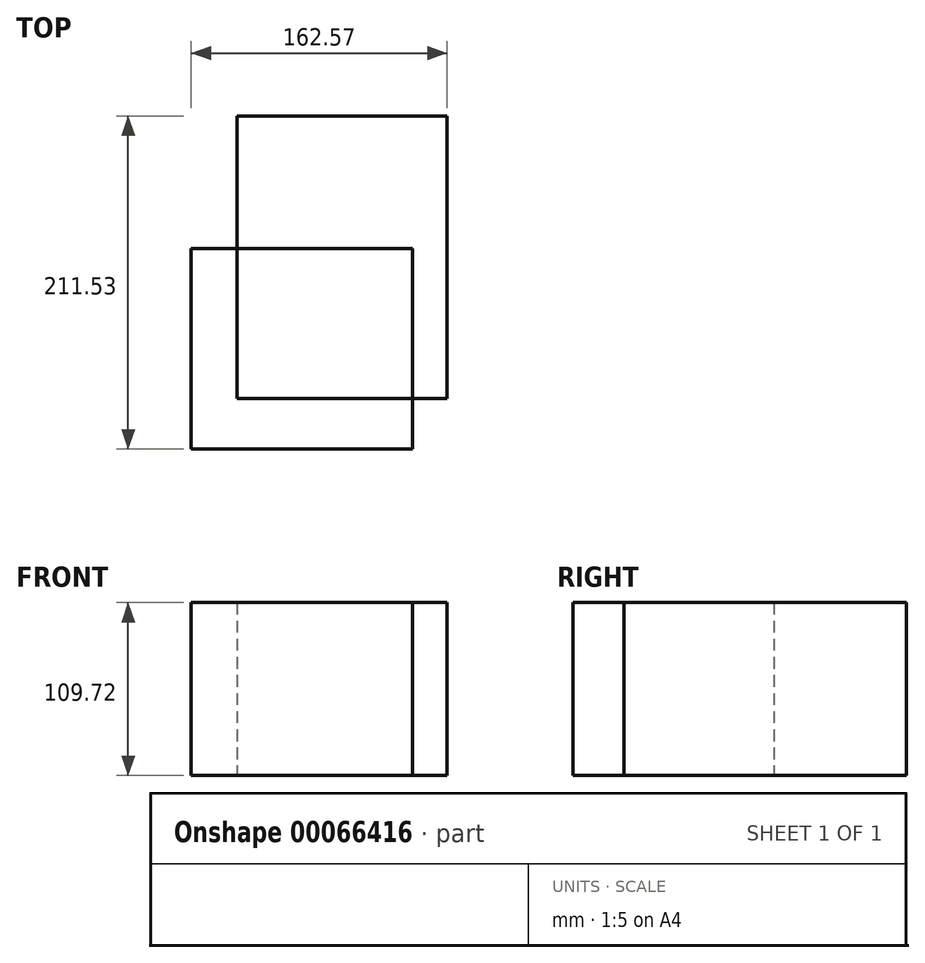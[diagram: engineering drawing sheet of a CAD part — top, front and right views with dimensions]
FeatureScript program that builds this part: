
annotation { "Feature Type Name" : "Feature", "Feature Type Description" : "" }
export const myFeature = defineFeature(function(context is Context, id is Id, definition is map)
    precondition{}
    {
        {
            var Q0;
            Q0=qCreatedBy(makeId("Top.planeOp"),FACE);
            var sketch = newSketch(context, id + "F0", { "sketchPlane" : qUnion([Q0])});
            skLineSegment(sketch, "E0.bottom", {"start": v(-140.53, -61.35) * mm, "end": v(0, -61.35) * mm});
            skLineSegment(sketch, "E0.top", {"start": v(-140.53, -188.84) * mm, "end": v(0, -188.84) * mm});
            skLineSegment(sketch, "E0.left", {"start": v(-140.53, -61.35) * mm, "end": v(-140.53, -188.84) * mm});
            skLineSegment(sketch, "E0.right", {"start": v(0, -61.35) * mm, "end": v(0, -188.84) * mm});
            skLineSegment(sketch, "E1.bottom", {"start": v(-111.48, -156.6) * mm, "end": v(22.04, -156.6) * mm});
            skLineSegment(sketch, "E1.top", {"start": v(-111.48, 22.7) * mm, "end": v(22.04, 22.7) * mm});
            skLineSegment(sketch, "E1.left", {"start": v(-111.48, -156.6) * mm, "end": v(-111.48, 22.7) * mm});
            skLineSegment(sketch, "E1.right", {"start": v(22.04, -156.6) * mm, "end": v(22.04, 22.7) * mm});
            skSolve(sketch);
        }
        {
            var Q0;
            {var subQ2=sQuery(id+"F0.wireOp",EDGE,"E0.top");Q0=makeQuery(id+"F0.imprint","IMPRINT",FACE,{"disambiguationData":[TD([[makeQuery(id+"F0.imprint","IMPRINT",EDGE,{"derivedFrom":subQ2}),1.0]])]});}
            var Q1;
            {var subQ0=sQuery(id+"F0.wireOp",EDGE,"E1.top");Q1=makeQuery(id+"F0.imprint","IMPRINT",FACE,{"disambiguationData":[TD([[makeQuery(id+"F0.imprint","IMPRINT",EDGE,{"derivedFrom":subQ0}),-1.0]])]});}
            extrude(context, id + "F1", {"entities" : qUnion([Q0, Q1]), "depth" : 109.72 * mm});
        }
    });
